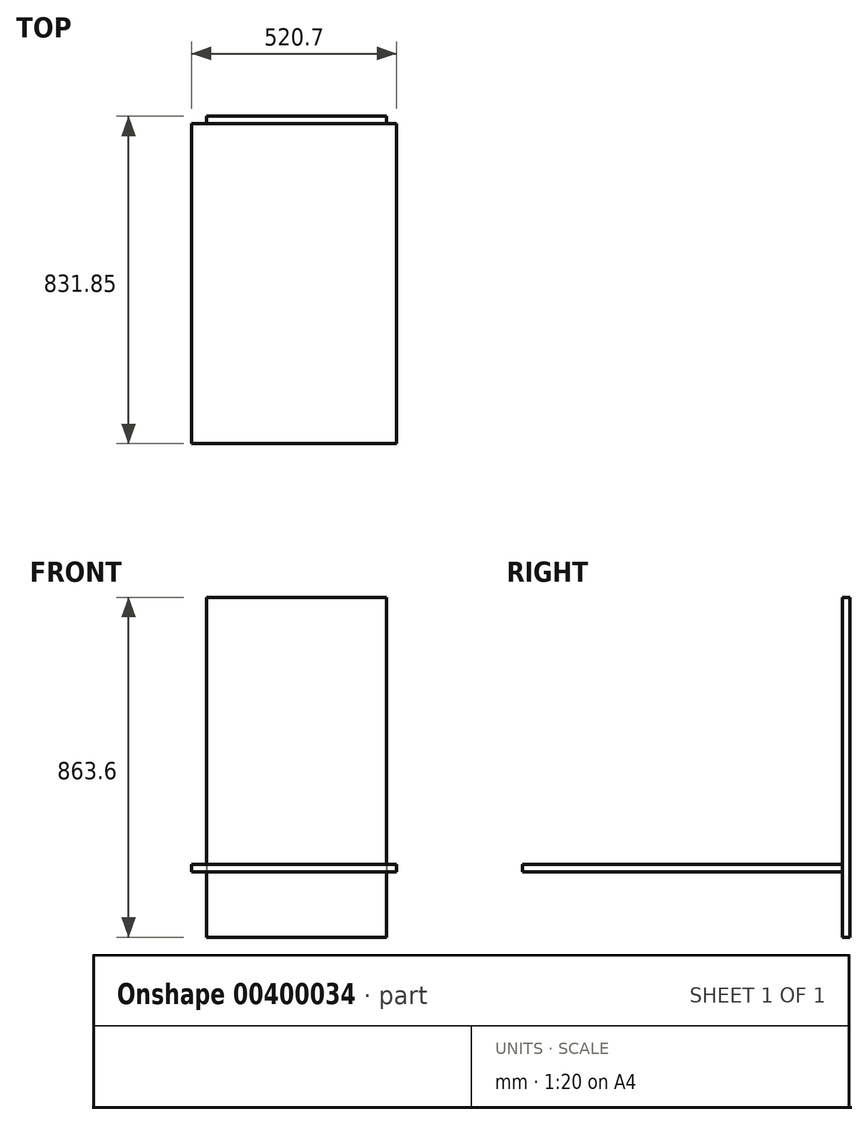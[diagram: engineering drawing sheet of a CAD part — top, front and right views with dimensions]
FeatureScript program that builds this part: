
annotation { "Feature Type Name" : "Feature", "Feature Type Description" : "" }
export const myFeature = defineFeature(function(context is Context, id is Id, definition is map)
    precondition{}
    {
        {
            var Q0;
            Q0=qCreatedBy(makeId("Top.planeOp"),FACE);
            var sketch = newSketch(context, id + "F0", { "sketchPlane" : qUnion([Q0])});
            skLineSegment(sketch, "E0.bottom", {"start": v(-464.25, 0) * mm, "end": v(56.45, 0) * mm});
            skLineSegment(sketch, "E0.top", {"start": v(-464.25, -812.8) * mm, "end": v(56.45, -812.8) * mm});
            skLineSegment(sketch, "E0.left", {"start": v(-464.25, 0) * mm, "end": v(-464.25, -812.8) * mm});
            skLineSegment(sketch, "E0.right", {"start": v(56.45, 0) * mm, "end": v(56.45, -812.8) * mm});
            skSolve(sketch);
        }
        {
            var Q0;
            Q0 = qSketchRegion(id + "F0", true);
            extrude(context, id + "F1", {"entities" : qUnion([Q0]), "depth" : 19.05 * mm});
        }
        {
            var Q0;
            Q0=qCreatedBy(makeId("Front.planeOp"),FACE);
            var sketch = newSketch(context, id + "F2", { "sketchPlane" : qUnion([Q0])});
            skLineSegment(sketch, "E1.bottom", {"start": v(-426.53, 697.5) * mm, "end": v(30.67, 697.5) * mm});
            skLineSegment(sketch, "E1.top", {"start": v(-426.53, -166.1) * mm, "end": v(30.67, -166.1) * mm});
            skLineSegment(sketch, "E1.left", {"start": v(-426.53, 697.5) * mm, "end": v(-426.53, -166.1) * mm});
            skLineSegment(sketch, "E1.right", {"start": v(30.67, 697.5) * mm, "end": v(30.67, -166.1) * mm});
            skSolve(sketch);
        }
        {
            var Q0;
            Q0=makeQuery(id+"F2.imprint","IMPRINT",FACE,{"disambiguationData":[TD([[makeQuery(id+"F2.imprint","IMPRINT",EDGE,{"derivedFrom":sQuery(id+"F2.wireOp",EDGE,"E1.bottom")}),-1.0]])]});
            extrude(context, id + "F3", {"entities" : qUnion([Q0]), "operationType" : NewBodyOperationType.ADD, "oppositeDirection" : true, "depth" : 19.05 * mm});
        }
    });
